# Revit family: 511_CA_HL-U_3-875-Nailfin
name_source: partatom
category: Windows
units: mm (PartAtom-declared; Revit-internal decimal feet)

## family parameters
Always vertical = Yes
Cut with Voids When Loaded = No
Host = Wall
OmniClass Number = 23.30.20.00
OmniClass Title = Windows
Room Calculation Point = No
Shared = No

## types (31) — shared parameters
Default Sill Height = 31 1/2"
MLW1 = 3 3/16"
Wall Closure = By host

## per-type parameters (varying)
| type | Bar set | Height | MLH | MLW2 | MLW3 | Width |
| 15.75x31Min | 21" | 31" | 10 1/2" | 3 9/16" | 2" | 15 3/4" |
| 36x72 | 54" | 72" | 27" | 3 9/16" | 4 1/2" | 36" |
| 42x120Max | 72" | 120" | 36" | 3 9/16" | 5 1/4" | 42" |
| 24x48 | 30" | 48" | 15" | 3 9/16" | 3" | 24" |
| 24x36 | 24" | 36" | 12" | 3 9/16" | 3" | 24" |
| 24x42 | 30" | 42" | 15" | 3 9/16" | 3" | 24" |
| 24x54 | 36" | 54" | 18" | 3 9/16" | 3" | 24" |
| 24x60 | 42" | 60" | 21" | 2 9/16" | 3" | 24" |
| 30x36 | 24" | 36" | 12" | 3 9/16" | 3 3/4" | 30" |
| 30x42 | 30" | 42" | 15" | 3 9/16" | 3 3/4" | 30" |
| 30x48 | 36" | 48" | 18" | 3 9/16" | 3 3/4" | 30" |
| 30x54 | 42" | 54" | 21" | 3 9/16" | 3 3/4" | 30" |
| 30x60 | 42" | 60" | 21" | 3 9/16" | 3 3/4" | 30" |
| 30x66 | 48" | 66" | 24" | 3 9/16" | 3 3/4" | 30" |
| 30x72 | 54" | 72" | 27" | 3 9/16" | 3 3/4" | 30" |
| 30x78 | 60" | 78" | 30" | 3 9/16" | 3 3/4" | 30" |
| 30x90 | 66" | 90" | 33" | 3 9/16" | 3 3/4" | 30" |
| 30x96 | 72" | 96" | 36" | 3 9/16" | 3 3/4" | 30" |
| 36x42 | 30" | 42" | 15" | 3 9/16" | 4 1/2" | 36" |
| 36x48 | 30" | 48" | 15" | 3 9/16" | 4 1/2" | 36" |
| 36x54 | 36" | 54" | 18" | 3 9/16" | 4 1/2" | 36" |
| 36x60 | 42" | 60" | 21" | 3 9/16" | 4 1/2" | 36" |
| 36x66 | 48" | 66" | 24" | 3 9/16" | 4 1/2" | 36" |
| 36x78 | 60" | 78" | 30" | 3 9/16" | 4 1/2" | 36" |
| 36x84 | 60" | 84" | 30" | 3 9/16" | 4 1/2" | 36" |
| 36x90 | 60" | 90" | 30" | 3 9/16" | 4 1/2" | 36" |
| 36x96 | 60" | 96" | 30" | 3 9/16" | 4 1/2" | 36" |
| 36x102 | 60" | 102" | 30" | 3 9/16" | 4 1/2" | 36" |
| 36x108 | 60" | 108" | 30" | 3 9/16" | 4 1/2" | 36" |
| 36x114 | 60" | 114" | 30" | 3 9/16" | 4 1/2" | 36" |
| 30x84 | 60" | 84" | 30" | 3 9/16" | 3 3/4" | 30" |

## geometry (parser evidence)
native form markers: Sweep x3
no freeform markers — native parametric forms only
